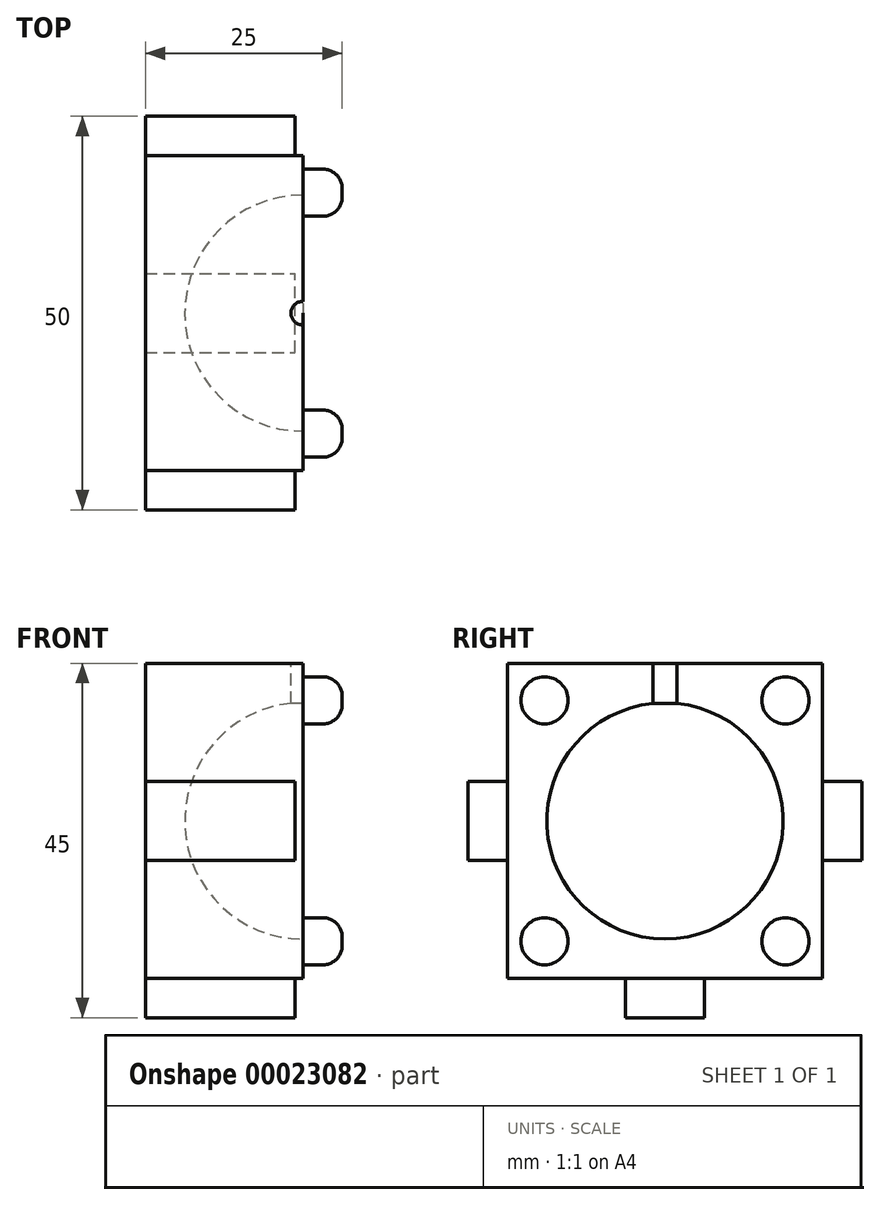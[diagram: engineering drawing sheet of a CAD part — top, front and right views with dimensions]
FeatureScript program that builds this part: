
annotation { "Feature Type Name" : "Feature", "Feature Type Description" : "" }
export const myFeature = defineFeature(function(context is Context, id is Id, definition is map)
    precondition{}
    {
        {
            var Q0;
            Q0=qCreatedBy(makeId("Front.planeOp"),FACE);
            var sketch = newSketch(context, id + "F0", { "sketchPlane" : qUnion([Q0])});
            skArc(sketch, "E0", {"start": v(-1.5, 14.92) * mm, "mid": v(-14.98, -0.75) * mm, "end": v(0, -15) * mm});
            skLineSegment(sketch, "E1", {"start": v(0, 15) * mm, "end": v(0, -15) * mm});
            skLineSegment(sketch, "E2", {"start": v(-1.5, 14.92) * mm, "end": v(-1.5, 35) * mm});
            skLineSegment(sketch, "E3", {"start": v(-1.5, 35) * mm, "end": v(0, 35) * mm});
            skLineSegment(sketch, "E4", {"start": v(0, 35) * mm, "end": v(0, 15) * mm});
            skSolve(sketch);
        }
        {
            var Q0;
            Q0=makeQuery(id+"F0.imprint","IMPRINT",FACE,{"disambiguationData":[TD([[makeQuery(id+"F0.imprint","IMPRINT",EDGE,{"derivedFrom":sQuery(id+"F0.wireOp",EDGE,"E0")}),1.0]])]});
            var Q1;
            Q1=sQuery(id+"F0.wireOp",EDGE,"E1");
            revolve(context, id + "F1", {"entities" : qUnion([Q0]), "axis" : qUnion([Q1]), "revolveType" : RevolveType.FULL});
        }
        {
            var Q0;
            Q0=qCreatedBy(makeId("Front.planeOp"),FACE);
            var sketch = newSketch(context, id + "F2", { "sketchPlane" : qUnion([Q0])});
            skLineSegment(sketch, "E5", {"start": v(0, 20) * mm, "end": v(-20, 20) * mm});
            skLineSegment(sketch, "E6", {"start": v(-20, 20) * mm, "end": v(-20, -20) * mm});
            skLineSegment(sketch, "E7", {"start": v(-20, -20) * mm, "end": v(0, -20) * mm});
            skLineSegment(sketch, "E8", {"start": v(0, -20) * mm, "end": v(0, 20) * mm});
            skPoint(sketch, "E9", {"position": v(0, 0) * mm});
            skPoint(sketch, "E10.end.orphan", {"position": v(-20, 0) * mm});
            skSolve(sketch);
        }
        {
            var Q0;
            Q0=qSketchRegion(id+"F2",true);
            extrude(context, id + "F3", {"entities" : qUnion([Q0]), "endBound" : BoundingType.SYMMETRIC, "depth" : 40 * mm});
        }
        {
            var Q0;
            Q0=makeQuery(id+"F1.opRevolve","SWEPT_BODY",BODY,{"disambiguationData":[OSD([sQuery(id+"F0.wireOp",EDGE,"E0"),sQuery(id+"F0.wireOp",EDGE,"E1"),sQuery(id+"F0.wireOp",EDGE,"E2"),sQuery(id+"F0.wireOp",EDGE,"E3"),sQuery(id+"F0.wireOp",EDGE,"E4")])]});
            var Q1;
            Q1=makeQuery(id+"F3.opExtrude","SWEPT_BODY",BODY,{"disambiguationData":[OSD([sQuery(id+"F2.wireOp",EDGE,"E5"),sQuery(id+"F2.wireOp",EDGE,"E6"),sQuery(id+"F2.wireOp",EDGE,"E7"),sQuery(id+"F2.wireOp",EDGE,"E8")])]});
            booleanBodies(context, id + "F4", {"operationType" : BooleanOperationType.SUBTRACTION, "tools" : qUnion([Q0]), "targets" : qUnion([Q1])});
        }
        {
            var Q0;
            Q0=makeQuery(id+"F3.opExtrude","SWEPT_FACE",FACE,{"disambiguationData":[OSD([sQuery(id+"F2.wireOp",EDGE,"E8")])]});
            var sketch = newSketch(context, id + "F5", { "sketchPlane" : qUnion([Q0])});
            skCircle(sketch, "E11", {"center": v(-15.3, 15.3) * mm, "radius": 3 * mm});
            skCircle(sketch, "E12", {"center": v(15.3, 15.3) * mm, "radius": 3 * mm});
            skCircle(sketch, "E13", {"center": v(15.3, -15.3) * mm, "radius": 3 * mm});
            skCircle(sketch, "E14", {"center": v(-15.3, -15.3) * mm, "radius": 3 * mm});
            skLineSegment(sketch, "E15", {"start": v(-20, 20) * mm, "end": v(20, -20) * mm, "construction": true});
            skLineSegment(sketch, "E16", {"start": v(20, 20) * mm, "end": v(-20, -20) * mm, "construction": true});
            skPoint(sketch, "E17", {"position": v(-10.6, 10.6) * mm});
            skLineSegment(sketch, "E18", {"start": v(-13.18, 17.42) * mm, "end": v(-17.42, 13.18) * mm, "construction": true});
            skPoint(sketch, "E19", {"position": v(10.6, 10.6) * mm});
            skLineSegment(sketch, "E20", {"start": v(-17.42, -13.18) * mm, "end": v(-13.18, -17.42) * mm, "construction": true});
            skLineSegment(sketch, "E21", {"start": v(13.18, -17.42) * mm, "end": v(17.42, -13.18) * mm, "construction": true});
            skLineSegment(sketch, "E22", {"start": v(13.18, 17.42) * mm, "end": v(17.42, 13.18) * mm, "construction": true});
            skPoint(sketch, "E23", {"position": v(-10.6, -10.6) * mm});
            skPoint(sketch, "E24", {"position": v(10.6, -10.6) * mm});
            skPoint(sketch, "E25", {"position": v(20, 20) * mm});
            skSolve(sketch);
        }
        {
            var Q0;
            Q0=makeQuery(id+"F5.imprint","IMPRINT",FACE,{"disambiguationData":[TD([[makeQuery(id+"F5.imprint","IMPRINT",EDGE,{"derivedFrom":sQuery(id+"F5.wireOp",EDGE,"E12")}),1.0]])]});
            var Q1;
            Q1=makeQuery(id+"F5.imprint","IMPRINT",FACE,{"disambiguationData":[TD([[makeQuery(id+"F5.imprint","IMPRINT",EDGE,{"derivedFrom":sQuery(id+"F5.wireOp",EDGE,"E13")}),1.0]])]});
            var Q2;
            Q2=makeQuery(id+"F5.imprint","IMPRINT",FACE,{"disambiguationData":[TD([[makeQuery(id+"F5.imprint","IMPRINT",EDGE,{"derivedFrom":sQuery(id+"F5.wireOp",EDGE,"E14")}),1.0]])]});
            var Q3;
            Q3=makeQuery(id+"F5.imprint","IMPRINT",FACE,{"disambiguationData":[TD([[makeQuery(id+"F5.imprint","IMPRINT",EDGE,{"derivedFrom":sQuery(id+"F5.wireOp",EDGE,"E11")}),1.0]])]});
            extrude(context, id + "F6", {"entities" : qUnion([Q0, Q1, Q2, Q3]), "operationType" : NewBodyOperationType.ADD, "depth" : 5 * mm});
        }
        {
            var Q0;
            Q0=makeQuery(id+"F6.opExtrude","CAP_EDGE",EDGE,{"disambiguationData":[OSD([sQuery(id+"F5.wireOp",EDGE,"E11")])],"isStart":false});
            var Q1;
            Q1=makeQuery(id+"F6.opExtrude","CAP_EDGE",EDGE,{"disambiguationData":[OSD([sQuery(id+"F5.wireOp",EDGE,"E12")])],"isStart":false});
            var Q2;
            Q2=makeQuery(id+"F6.opExtrude","CAP_EDGE",EDGE,{"disambiguationData":[OSD([sQuery(id+"F5.wireOp",EDGE,"E13")])],"isStart":false});
            var Q3;
            Q3=makeQuery(id+"F6.opExtrude","CAP_EDGE",EDGE,{"disambiguationData":[OSD([sQuery(id+"F5.wireOp",EDGE,"E14")])],"isStart":false});
            fillet(context, id + "F7", {"entities" : qUnion([Q0, Q1, Q2, Q3]), "radius" : 2.5 * mm, "tangentPropagation" : true, "allowEdgeOverflow" : false});
        }
        {
            var Q0;
            Q0=makeQuery(id+"F3.opExtrude","CAP_FACE",FACE,{"disambiguationData":[OSD([sQuery(id+"F2.wireOp",EDGE,"E5"),sQuery(id+"F2.wireOp",EDGE,"E6"),sQuery(id+"F2.wireOp",EDGE,"E7"),sQuery(id+"F2.wireOp",EDGE,"E8")])],"isStart":false});
            var sketch = newSketch(context, id + "F8", { "sketchPlane" : qUnion([Q0])});
            skLineSegment(sketch, "E26.bottom", {"start": v(-20, 5) * mm, "end": v(-1, 5) * mm});
            skLineSegment(sketch, "E26.top", {"start": v(-20, -5) * mm, "end": v(-1, -5) * mm});
            skLineSegment(sketch, "E26.left", {"start": v(-20, 5) * mm, "end": v(-20, -5) * mm});
            skLineSegment(sketch, "E26.right", {"start": v(-1, 5) * mm, "end": v(-1, -5) * mm});
            skSolve(sketch);
        }
        {
            var Q0;
            Q0=qSketchRegion(id+"F8",true);
            extrude(context, id + "F9", {"entities" : qUnion([Q0]), "operationType" : NewBodyOperationType.ADD, "depth" : 5 * mm});
        }
        {
            var Q0;
            Q0=makeQuery(id+"F3.opExtrude","SWEPT_FACE",FACE,{"disambiguationData":[OSD([sQuery(id+"F2.wireOp",EDGE,"E7")])]});
            var sketch = newSketch(context, id + "F10", { "sketchPlane" : qUnion([Q0])});
            skLineSegment(sketch, "E27.bottom", {"start": v(-20, 5) * mm, "end": v(-1, 5) * mm});
            skLineSegment(sketch, "E27.top", {"start": v(-20, -5) * mm, "end": v(-1, -5) * mm});
            skLineSegment(sketch, "E27.left", {"start": v(-20, 5) * mm, "end": v(-20, -5) * mm});
            skLineSegment(sketch, "E27.right", {"start": v(-1, 5) * mm, "end": v(-1, -5) * mm});
            skSolve(sketch);
        }
        {
            var Q0;
            Q0=qSketchRegion(id+"F10",true);
            extrude(context, id + "F11", {"entities" : qUnion([Q0]), "operationType" : NewBodyOperationType.ADD, "depth" : 5 * mm});
        }
        {
            var Q0;
            Q0=makeQuery(id+"F3.opExtrude","CAP_FACE",FACE,{"disambiguationData":[OSD([sQuery(id+"F2.wireOp",EDGE,"E5"),sQuery(id+"F2.wireOp",EDGE,"E6"),sQuery(id+"F2.wireOp",EDGE,"E7"),sQuery(id+"F2.wireOp",EDGE,"E8")])],"isStart":true});
            var sketch = newSketch(context, id + "F12", { "sketchPlane" : qUnion([Q0])});
            skLineSegment(sketch, "E28.bottom", {"start": v(1, 5) * mm, "end": v(20, 5) * mm});
            skLineSegment(sketch, "E28.top", {"start": v(1, -5) * mm, "end": v(20, -5) * mm});
            skLineSegment(sketch, "E28.left", {"start": v(1, 5) * mm, "end": v(1, -5) * mm});
            skLineSegment(sketch, "E28.right", {"start": v(20, 5) * mm, "end": v(20, -5) * mm});
            skSolve(sketch);
        }
        {
            var Q0;
            Q0=qSketchRegion(id+"F12",true);
            extrude(context, id + "F13", {"entities" : qUnion([Q0]), "operationType" : NewBodyOperationType.ADD, "depth" : 5 * mm});
        }
    });
